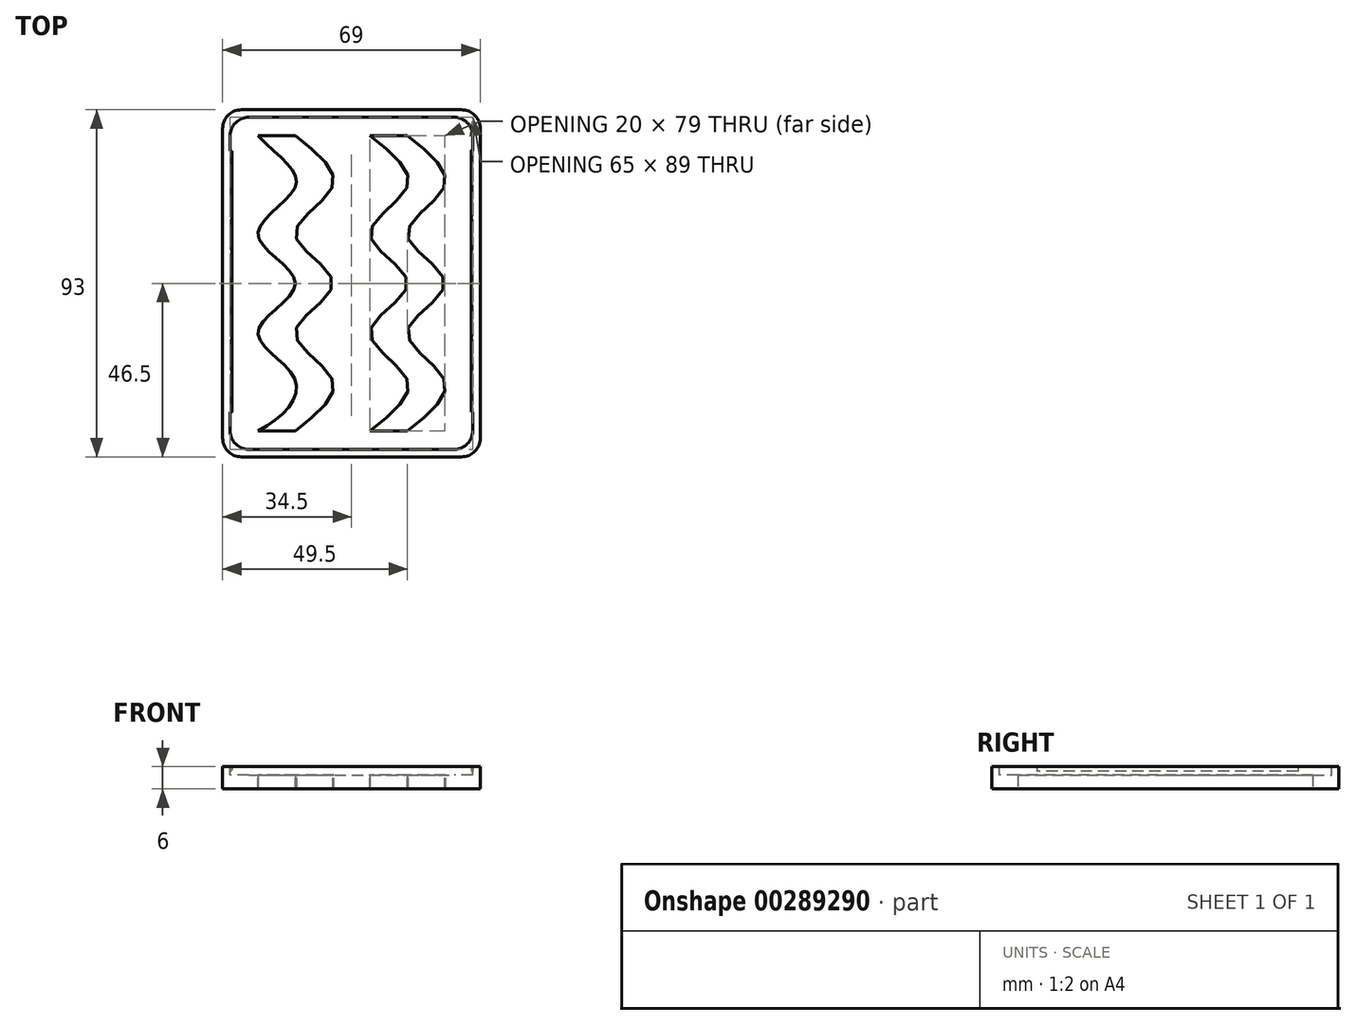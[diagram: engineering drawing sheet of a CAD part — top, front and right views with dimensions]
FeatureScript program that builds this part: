
annotation { "Feature Type Name" : "Feature", "Feature Type Description" : "" }
export const myFeature = defineFeature(function(context is Context, id is Id, definition is map)
    precondition{}
    {
        {
            var Q0;
            Q0=qCreatedBy(makeId("Top.planeOp"),FACE);
            var sketch = newSketch(context, id + "F0", { "sketchPlane" : qUnion([Q0])});
            skLineSegment(sketch, "E0.bottom", {"start": v(0, 0) * mm, "end": v(69, 0) * mm});
            skLineSegment(sketch, "E0.top", {"start": v(0, -93) * mm, "end": v(69, -93) * mm});
            skLineSegment(sketch, "E0.left", {"start": v(0, 0) * mm, "end": v(0, -93) * mm});
            skLineSegment(sketch, "E0.right", {"start": v(69, 0) * mm, "end": v(69, -93) * mm});
            skSolve(sketch);
        }
        {
            var Q0;
            Q0 = qSketchRegion(id + "F0", true);
            extrude(context, id + "F1", {"entities" : qUnion([Q0]), "depth" : 6 * mm});
        }
        {
            var Q0;
            Q0=makeQuery(id+"F1.opExtrude","CAP_FACE",FACE,{"disambiguationData":[OSD([sQuery(id+"F0.wireOp",EDGE,"E0.bottom"),sQuery(id+"F0.wireOp",EDGE,"E0.top"),sQuery(id+"F0.wireOp",EDGE,"E0.left"),sQuery(id+"F0.wireOp",EDGE,"E0.right")])],"isStart":false});
            var sketch = newSketch(context, id + "F2", { "sketchPlane" : qUnion([Q0])});
            skLineSegment(sketch, "E1.bottom", {"start": v(2, -2) * mm, "end": v(67, -2) * mm});
            skLineSegment(sketch, "E1.top", {"start": v(2, -91) * mm, "end": v(67, -91) * mm});
            skLineSegment(sketch, "E1.left", {"start": v(2, -2) * mm, "end": v(2, -91) * mm});
            skLineSegment(sketch, "E1.right", {"start": v(67, -2) * mm, "end": v(67, -91) * mm});
            skSolve(sketch);
        }
        {
            var Q0;
            Q0 = qSketchRegion(id + "F2", true);
            extrude(context, id + "F3", {"entities" : qUnion([Q0]), "operationType" : NewBodyOperationType.REMOVE, "oppositeDirection" : true, "depth" : 2.3 * mm});
        }
        {
            var Q0;
            Q0=makeQuery(id+"F3.boolean.opBoolean","COPY",FACE,{"derivedFrom":makeQuery(id+"F3.opExtrude","SWEPT_FACE",FACE,{"disambiguationData":[OSD([sQuery(id+"F2.wireOp",EDGE,"E1.top")])]})});
            cPlane(context, id + "F4", {"entities" : qUnion([Q0]), "cplaneType" : CPlaneType.OFFSET, "offset" : 10 * mm, "width" : 150 * mm, "height" : 150 * mm});
        }
        {
            var Q0;
            Q0=makeQuery(id+"F3.boolean.opBoolean","COPY",FACE,{"derivedFrom":makeQuery(id+"F3.opExtrude","SWEPT_FACE",FACE,{"disambiguationData":[OSD([sQuery(id+"F2.wireOp",EDGE,"E1.right")])]})});
            var Q1;
            Q1=makeQuery(id+"F3.boolean.opBoolean","COPY",FACE,{"derivedFrom":makeQuery(id+"F3.opExtrude","SWEPT_FACE",FACE,{"disambiguationData":[OSD([sQuery(id+"F2.wireOp",EDGE,"E1.left")])]})});
            cPlane(context, id + "F5", {"entities" : qUnion([Q0, Q1]), "cplaneType" : CPlaneType.MID_PLANE, "offset" : 25 * mm, "width" : 150 * mm, "height" : 150 * mm});
        }
        {
            var Q0;
            Q0=qCreatedBy(id+"F4.planeOp",FACE);
            var sketch = newSketch(context, id + "F6", { "sketchPlane" : qUnion([Q0])});
            skLineSegment(sketch, "E2.0.1", {"start": v(-2, 6) * mm, "end": v(-2, 3.7) * mm});
            skLineSegment(sketch, "E2.0.3", {"start": v(-2, 3.7) * mm, "end": v(-2, 6) * mm});
            skLineSegment(sketch, "E3.MirrorCS", {"start": v(-67, 6) * mm, "end": v(-67, 3.7) * mm});
            skLineSegment(sketch, "E4.MirrorCS", {"start": v(-67, 3.7) * mm, "end": v(-67, 6) * mm});
            skArc(sketch, "E5", {"start": v(-2, 6) * mm, "mid": v(-2.3, 5.88) * mm, "end": v(-2.42, 5.58) * mm});
            skArc(sketch, "E6", {"start": v(-2.42, 5.15) * mm, "mid": v(-2.3, 4.85) * mm, "end": v(-2, 4.72) * mm});
            skLineSegment(sketch, "E7", {"start": v(-2.42, 5.58) * mm, "end": v(-2.42, 5.15) * mm});
            skLineSegment(sketch, "E8.MirrorCS", {"start": v(-66.58, 5.58) * mm, "end": v(-66.58, 5.15) * mm});
            skArc(sketch, "E9.MirrorCS", {"start": v(-67, 6) * mm, "mid": v(-66.7, 5.88) * mm, "end": v(-66.58, 5.58) * mm});
            skArc(sketch, "E10.MirrorCS", {"start": v(-66.58, 5.15) * mm, "mid": v(-66.7, 4.85) * mm, "end": v(-67, 4.72) * mm});
            skSolve(sketch);
        }
        {
            var Q0;
            Q0 = qSketchRegion(id + "F6", true);
            extrude(context, id + "F7", {"entities" : qUnion([Q0]), "operationType" : NewBodyOperationType.ADD, "depth" : 70 * mm});
        }
        {
            var Q0;
            Q0=makeQuery(id+"F1.opExtrude","CAP_FACE",FACE,{"disambiguationData":[OSD([sQuery(id+"F0.wireOp",EDGE,"E0.bottom"),sQuery(id+"F0.wireOp",EDGE,"E0.top"),sQuery(id+"F0.wireOp",EDGE,"E0.left"),sQuery(id+"F0.wireOp",EDGE,"E0.right")])],"isStart":true});
            var sketch = newSketch(context, id + "F8", { "sketchPlane" : qUnion([Q0])});
            skLineSegment(sketch, "E11", {"start": v(9.5, 7) * mm, "end": v(19.5, 7) * mm});
            skLineSegment(sketch, "E12", {"start": v(19.5, 86) * mm, "end": v(9.5, 86) * mm});
            skFitSpline(sketch, "E13", {"points": [v(9.5, 86) * mm, v(19.5, 72.5) * mm, v(9.5, 59.5) * mm, v(19.5, 46.5) * mm, v(9.5, 33.5) * mm, v(19.5, 20.5) * mm, v(9.5, 7) * mm], "startDerivative": vector(112.27, -53.77) * mm, "endDerivative": vector(-97.73, -99.2) * mm});
            skPoint(sketch, "E14.5.internal.snap0", {"position": v(29.5, 46.5) * mm});
            skFitSpline(sketch, "E14", {"points": [v(19.5, 86) * mm, v(29.5, 72.5) * mm, v(19.5, 59.5) * mm, v(29.5, 46.5) * mm, v(19.5, 33.5) * mm, v(29.5, 20.5) * mm, v(19.5, 7) * mm], "startDerivative": vector(103.6, -80.9) * mm, "endDerivative": vector(-103.6, -80.9) * mm});
            skFitSpline(sketch, "E15", {"points": [v(39.5, 86) * mm, v(49.5, 72.5) * mm, v(39.5, 59.5) * mm, v(49.5, 46.5) * mm, v(39.5, 33.5) * mm, v(49.5, 20.5) * mm, v(39.5, 7) * mm], "startDerivative": vector(103.6, -80.9) * mm, "endDerivative": vector(-103.6, -80.9) * mm});
            skFitSpline(sketch, "E16", {"points": [v(49.5, 86) * mm, v(59.5, 72.5) * mm, v(49.5, 59.5) * mm, v(59.5, 46.5) * mm, v(49.5, 33.5) * mm, v(59.5, 20.5) * mm, v(49.5, 7) * mm], "startDerivative": vector(103.6, -80.9) * mm, "endDerivative": vector(-103.6, -80.9) * mm});
            skLineSegment(sketch, "E17", {"start": v(39.5, 86) * mm, "end": v(49.5, 86) * mm});
            skLineSegment(sketch, "E18", {"start": v(49.5, 7) * mm, "end": v(39.5, 7) * mm});
            skLineSegment(sketch, "E19.trimOffspring", {"start": v(19.5, 46.5) * mm, "end": v(19.5, 46.52) * mm});
            skPoint(sketch, "E20.start.orphan", {"position": v(29.5, 7) * mm});
            skPoint(sketch, "E21.end.orphan", {"position": v(29.5, 86) * mm});
            skPoint(sketch, "E22.orphan", {"position": v(59.5, 86) * mm});
            skPoint(sketch, "E23.start.orphan", {"position": v(59.5, 7) * mm});
            skPoint(sketch, "E24.0.0.end.orphan", {"position": v(2, 81) * mm});
            skPoint(sketch, "E24.0.0.start.orphan", {"position": v(2, 11) * mm});
            skPoint(sketch, "E24.0.2.start.orphan", {"position": v(2, 81) * mm});
            skPoint(sketch, "E25.0.2.end.orphan", {"position": v(2, 91) * mm});
            skPoint(sketch, "E25.0.0.start.orphan", {"position": v(2, 91) * mm});
            skPoint(sketch, "E26.0.7.end.orphan", {"position": v(67, 81) * mm});
            skPoint(sketch, "E26.0.7.start.orphan", {"position": v(67, 91) * mm});
            skPoint(sketch, "E26.0.1.end.orphan", {"position": v(67, 11) * mm});
            skPoint(sketch, "E26.0.1.start.orphan", {"position": v(67, 81) * mm});
            skPoint(sketch, "E26.0.3.start.orphan", {"position": v(67, 11) * mm});
            skPoint(sketch, "E27.0.2.end.orphan", {"position": v(67, 2) * mm});
            skPoint(sketch, "E27.0.0.start.orphan", {"position": v(67, 2) * mm});
            skPoint(sketch, "E24.0.6.end.orphan", {"position": v(2, 11) * mm});
            skPoint(sketch, "E24.0.6.start.orphan", {"position": v(2, 2) * mm});
            skSolve(sketch);
        }
        {
            var Q0;
            {var subQ1=sQuery(id+"F8.wireOp",EDGE,"E11");Q0=makeQuery(id+"F8.imprint","IMPRINT",FACE,{"disambiguationData":[TD([[makeQuery(id+"F8.imprint","IMPRINT",EDGE,{"derivedFrom":subQ1}),1.0]])]});}
            var Q1;
            Q1=makeQuery(id+"F8.imprint","IMPRINT",FACE,{"disambiguationData":[TD([[makeQuery(id+"F8.imprint","IMPRINT",EDGE,{"derivedFrom":sQuery(id+"F8.wireOp",EDGE,"E15")}),1.0]])]});
            extrude(context, id + "F9", {"entities" : qUnion([Q0, Q1]), "operationType" : NewBodyOperationType.REMOVE, "oppositeDirection" : true, "depth" : 25 * mm});
        }
        {
            var Q0;
            Q0=makeQuery(id+"F1.opExtrude","SWEPT_EDGE",EDGE,{"disambiguationData":[OSD([sQuery(id+"F0.wireOp",EDGE,"E0.bottom"),sQuery(id+"F0.wireOp",EDGE,"E0.right")])]});
            var Q1;
            Q1=makeQuery(id+"F1.opExtrude","SWEPT_EDGE",EDGE,{"disambiguationData":[OSD([sQuery(id+"F0.wireOp",EDGE,"E0.bottom"),sQuery(id+"F0.wireOp",EDGE,"E0.left")])]});
            var Q2;
            Q2=makeQuery(id+"F1.opExtrude","SWEPT_EDGE",EDGE,{"disambiguationData":[OSD([sQuery(id+"F0.wireOp",EDGE,"E0.top"),sQuery(id+"F0.wireOp",EDGE,"E0.left")])]});
            var Q3;
            Q3=makeQuery(id+"F1.opExtrude","SWEPT_EDGE",EDGE,{"disambiguationData":[OSD([sQuery(id+"F0.wireOp",EDGE,"E0.top"),sQuery(id+"F0.wireOp",EDGE,"E0.right")])]});
            fillet(context, id + "F10", {"entities" : qUnion([Q0, Q1, Q2, Q3]), "radius" : 5 * mm, "tangentPropagation" : true, "allowEdgeOverflow" : false});
        }
        {
            var Q0;
            Q0=makeQuery(id+"F3.boolean.opBoolean","COPY",EDGE,{"derivedFrom":makeQuery(id+"F3.opExtrude","SWEPT_EDGE",EDGE,{"disambiguationData":[OSD([sQuery(id+"F2.wireOp",EDGE,"E1.top"),sQuery(id+"F2.wireOp",EDGE,"E1.left")])]})});
            var Q1;
            Q1=makeQuery(id+"F3.boolean.opBoolean","COPY",EDGE,{"derivedFrom":makeQuery(id+"F3.opExtrude","SWEPT_EDGE",EDGE,{"disambiguationData":[OSD([sQuery(id+"F2.wireOp",EDGE,"E1.top"),sQuery(id+"F2.wireOp",EDGE,"E1.right")])]})});
            var Q2;
            Q2=makeQuery(id+"F3.boolean.opBoolean","COPY",EDGE,{"derivedFrom":makeQuery(id+"F3.opExtrude","SWEPT_EDGE",EDGE,{"disambiguationData":[OSD([sQuery(id+"F2.wireOp",EDGE,"E1.bottom"),sQuery(id+"F2.wireOp",EDGE,"E1.left")])]})});
            var Q3;
            Q3=makeQuery(id+"F3.boolean.opBoolean","COPY",EDGE,{"derivedFrom":makeQuery(id+"F3.opExtrude","SWEPT_EDGE",EDGE,{"disambiguationData":[OSD([sQuery(id+"F2.wireOp",EDGE,"E1.bottom"),sQuery(id+"F2.wireOp",EDGE,"E1.right")])]})});
            fillet(context, id + "F11", {"entities" : qUnion([Q0, Q1, Q2, Q3]), "radius" : 5 * mm, "tangentPropagation" : true, "allowEdgeOverflow" : false});
        }
    });
